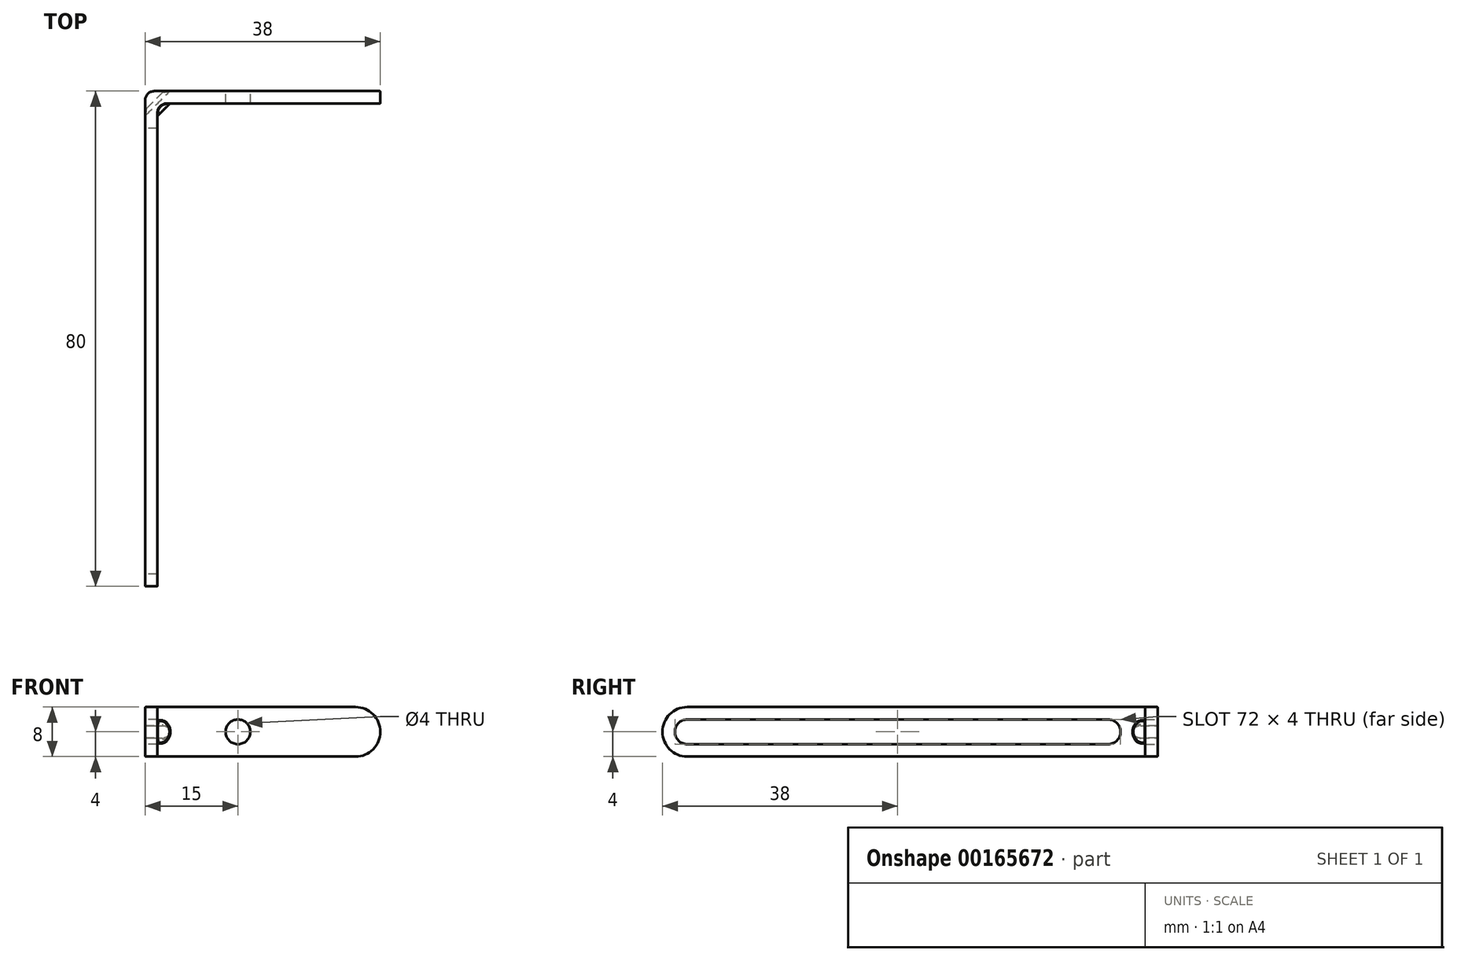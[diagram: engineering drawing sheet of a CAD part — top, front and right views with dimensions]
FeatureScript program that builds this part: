
annotation { "Feature Type Name" : "Feature", "Feature Type Description" : "" }
export const myFeature = defineFeature(function(context is Context, id is Id, definition is map)
    precondition{}
    {
        {
            var Q0;
            Q0=qCreatedBy(makeId("Top.planeOp"),FACE);
            var sketch = newSketch(context, id + "F0", { "sketchPlane" : qUnion([Q0])});
            skLineSegment(sketch, "E0", {"start": v(0, 0) * mm, "end": v(0, 80) * mm});
            skLineSegment(sketch, "E1", {"start": v(0, 80) * mm, "end": v(38, 80) * mm});
            skLineSegment(sketch, "E2.0", {"start": v(2, 78) * mm, "end": v(38, 78) * mm});
            skLineSegment(sketch, "E2.1", {"start": v(2, 0) * mm, "end": v(2, 78) * mm});
            skLineSegment(sketch, "E3", {"start": v(38, 80) * mm, "end": v(38, 78) * mm});
            skLineSegment(sketch, "E4", {"start": v(2, 0) * mm, "end": v(0, 0) * mm});
            skSolve(sketch);
        }
        {
            var Q0;
            Q0=makeQuery(id+"F0.imprint","IMPRINT",FACE,{"disambiguationData":[TD([[makeQuery(id+"F0.imprint","IMPRINT",EDGE,{"derivedFrom":sQuery(id+"F0.wireOp",EDGE,"E0")}),-1.0]])]});
            var Q1;
            Q1=sQuery(id+"F0.wireOp",EDGE,"E1");
            extrude(context, id + "F1", {"entities" : qUnion([Q0]), "surfaceEntities" : qUnion([Q1]), "endBound" : BoundingType.SYMMETRIC, "depth" : 8 * mm, "offsetDistance" : 25 * mm});
        }
        {
            var Q0;
            Q0=makeQuery(id+"F1.opExtrude","CAP_EDGE",EDGE,{"disambiguationData":[OSD([sQuery(id+"F0.wireOp",EDGE,"E4")])],"isStart":false});
            var Q1;
            Q1=makeQuery(id+"F1.opExtrude","CAP_EDGE",EDGE,{"disambiguationData":[OSD([sQuery(id+"F0.wireOp",EDGE,"E4")])],"isStart":true});
            var Q2;
            Q2=makeQuery(id+"F1.opExtrude","CAP_EDGE",EDGE,{"disambiguationData":[OSD([sQuery(id+"F0.wireOp",EDGE,"E3")])],"isStart":false});
            var Q3;
            Q3=makeQuery(id+"F1.opExtrude","CAP_EDGE",EDGE,{"disambiguationData":[OSD([sQuery(id+"F0.wireOp",EDGE,"E3")])],"isStart":true});
            fillet(context, id + "F2", {"entities" : qUnion([Q0, Q1, Q2, Q3]), "tangentPropagation" : true, "radius" : 4 * mm, "defaultsChanged" : true, "vertexSettings" : []});
        }
        {
            var Q0;
            Q0=makeQuery(id+"F1.opExtrude","SWEPT_EDGE",EDGE,{"disambiguationData":[OSD([sQuery(id+"F0.wireOp",EDGE,"E2.0"),sQuery(id+"F0.wireOp",EDGE,"E2.1")])]});
            var Q1;
            Q1=makeQuery(id+"F1.opExtrude","SWEPT_EDGE",EDGE,{"disambiguationData":[OSD([sQuery(id+"F0.wireOp",EDGE,"E0"),sQuery(id+"F0.wireOp",EDGE,"E1")])]});
            fillet(context, id + "F3", {"entities" : qUnion([Q0, Q1]), "tangentPropagation" : true, "radius" : 1.5 * mm, "defaultsChanged" : false, "vertexSettings" : []});
        }
        {
            var Q0;
            Q0=makeQuery(id+"F1.opExtrude","SWEPT_FACE",FACE,{"disambiguationData":[OSD([sQuery(id+"F0.wireOp",EDGE,"E0")])]});
            var sketch = newSketch(context, id + "F4", { "sketchPlane" : qUnion([Q0])});
            skCircle(sketch, "E5", {"center": v(-4, 0) * mm, "radius": 2 * mm});
            skCircle(sketch, "E6", {"center": v(-72, 0) * mm, "radius": 2 * mm});
            skLineSegment(sketch, "E7", {"start": v(-72, 2) * mm, "end": v(-4, 2) * mm});
            skLineSegment(sketch, "E8", {"start": v(-4, -2) * mm, "end": v(-72, -2) * mm});
            skLineSegment(sketch, "E9", {"start": v(6.38, 0) * mm, "end": v(-88.71, 0) * mm, "construction": true});
            skSolve(sketch);
        }
        {
            var Q0;
            Q0 = qSketchRegion(id + "F4", true);
            extrude(context, id + "F5", {"entities" : qUnion([Q0]), "operationType" : NewBodyOperationType.REMOVE, "endBound" : BoundingType.UP_TO_NEXT, "oppositeDirection" : true, "depth" : 25 * mm, "offsetDistance" : 25 * mm});
        }
        {
            var Q0;
            Q0=makeQuery(id+"F1.opExtrude","SWEPT_FACE",FACE,{"disambiguationData":[OSD([sQuery(id+"F0.wireOp",EDGE,"E1")])]});
            var sketch = newSketch(context, id + "F6", { "sketchPlane" : qUnion([Q0])});
            skLineSegment(sketch, "E10.bottom", {"start": v(3, 1) * mm, "end": v(-3, 1) * mm});
            skLineSegment(sketch, "E10.top", {"start": v(3, -1) * mm, "end": v(-3, -1) * mm});
            skLineSegment(sketch, "E10.left", {"start": v(4, 0) * mm, "end": v(4, 0) * mm});
            skLineSegment(sketch, "E10.right", {"start": v(-4, 0) * mm, "end": v(-4, 0) * mm});
            skPoint(sketch, "E10.middle", {"position": v(0, 0) * mm});
            skPoint(sketch, "E11.visualSharp", {"position": v(4, 1) * mm});
            skArc(sketch, "E11.filletArc", {"start": v(4, 0) * mm, "mid": v(3.7, 0.7) * mm, "end": v(3, 1) * mm});
            skPoint(sketch, "E12.visualSharp", {"position": v(-4, 1) * mm});
            skArc(sketch, "E12.filletArc", {"start": v(-3, 1) * mm, "mid": v(-3.7, 0.7) * mm, "end": v(-4, 0) * mm});
            skPoint(sketch, "E13.visualSharp", {"position": v(-4, -1) * mm});
            skArc(sketch, "E13.filletArc", {"start": v(-4, 0) * mm, "mid": v(-3.7, -0.7) * mm, "end": v(-3, -1) * mm});
            skPoint(sketch, "E14.visualSharp", {"position": v(4, -1) * mm});
            skArc(sketch, "E14.filletArc", {"start": v(3, -1) * mm, "mid": v(3.7, -0.7) * mm, "end": v(4, 0) * mm});
            skSolve(sketch);
        }
        {
            var Q0;
            Q0 = qSketchRegion(id + "F6", true);
            extrude(context, id + "F7", {"entities" : qUnion([Q0]), "oppositeDirection" : true, "depth" : 4 * mm, "offsetDistance" : 25 * mm});
        }
        {
            var Q0;
            Q0=makeQuery(id+"F7.opExtrude","CAP_EDGE",EDGE,{"disambiguationData":[OSD([sQuery(id+"F6.wireOp",EDGE,"E10.bottom")])],"isStart":false});
            var Q1;
            Q1=makeQuery(id+"F7.opExtrude","CAP_EDGE",EDGE,{"disambiguationData":[OSD([sQuery(id+"F6.wireOp",EDGE,"E10.top")])],"isStart":false});
            fillet(context, id + "F8", {"entities" : qUnion([Q0, Q1]), "radius" : 1 * mm, "defaultsChanged" : true, "vertexSettings" : []});
        }
        {
            var Q0;
            Q0=makeQuery(id+"F7.opExtrude","SWEPT_BODY",BODY,{"disambiguationData":[OSD([sQuery(id+"F6.wireOp",EDGE,"E10.bottom"),sQuery(id+"F6.wireOp",EDGE,"E10.top"),sQuery(id+"F6.wireOp",EDGE,"E11.filletArc"),sQuery(id+"F6.wireOp",EDGE,"E12.filletArc"),sQuery(id+"F6.wireOp",EDGE,"E13.filletArc"),sQuery(id+"F6.wireOp",EDGE,"E14.filletArc")])]});
            var Q1;
            Q1=makeQuery(id+"F1.opExtrude","SWEPT_BODY",BODY,{"disambiguationData":[OSD([sQuery(id+"F0.wireOp",EDGE,"E0"),sQuery(id+"F0.wireOp",EDGE,"E1"),sQuery(id+"F0.wireOp",EDGE,"E2.0"),sQuery(id+"F0.wireOp",EDGE,"E2.1"),sQuery(id+"F0.wireOp",EDGE,"E3"),sQuery(id+"F0.wireOp",EDGE,"E4")])]});
            booleanBodies(context, id + "F9", {"operationType" : BooleanOperationType.SUBTRACTION, "tools" : qUnion([Q0]), "targets" : qUnion([Q1])});
        }
        {
            var Q0;
            Q0=makeQuery(id+"F1.opExtrude","SWEPT_FACE",FACE,{"disambiguationData":[OSD([sQuery(id+"F0.wireOp",EDGE,"E0")])]});
            var sketch = newSketch(context, id + "F10", { "sketchPlane" : qUnion([Q0])});
            skArc(sketch, "E15.0", {"start": v(-77, -1) * mm, "mid": v(-76, 0) * mm, "end": v(-77, 1) * mm});
            skLineSegment(sketch, "E16", {"start": v(-77.2, 0) * mm, "end": v(-73.29, 0) * mm, "construction": true});
            skLineSegment(sketch, "E17", {"start": v(-77, 2.15) * mm, "end": v(-77, -2.41) * mm, "construction": true});
            skLineSegment(sketch, "E18", {"start": v(-77, 1) * mm, "end": v(-77, 2) * mm});
            skLineSegment(sketch, "E19", {"start": v(-77, 2) * mm, "end": v(-74.95, 2) * mm, "construction": true});
            skLineSegment(sketch, "E20", {"start": v(-77, -1) * mm, "end": v(-77, -2) * mm});
            skLineSegment(sketch, "E21", {"start": v(-77, 2) * mm, "end": v(-76, 2) * mm});
            skArc(sketch, "E22", {"start": v(-74, 0) * mm, "mid": v(-74.59, 1.41) * mm, "end": v(-76, 2) * mm});
            skArc(sketch, "E23.MirrorCS", {"start": v(-74, 0) * mm, "mid": v(-74.59, -1.41) * mm, "end": v(-76, -2) * mm});
            skLineSegment(sketch, "E24.MirrorCS", {"start": v(-77, -2) * mm, "end": v(-76, -2) * mm});
            skSolve(sketch);
        }
        {
            var Q0;
            {var subQ0=sQuery(id+"F6.wireOp",EDGE,"E12.filletArc");Q0=makeQuery(id+"F6.imprint","IMPRINT",FACE,{"disambiguationData":[TD([[makeQuery(id+"F6.imprint","IMPRINT",EDGE,{"derivedFrom":subQ0}),-1.0]])]});}
            var sketch = newSketch(context, id + "F11", { "sketchPlane" : qUnion([Q0])});
            skLineSegment(sketch, "E25", {"start": v(-3, -7.44) * mm, "end": v(-3, 4.7) * mm, "construction": true});
            skLineSegment(sketch, "E26", {"start": v(-1.82, 0) * mm, "end": v(-6.7, 0) * mm, "construction": true});
            skArc(sketch, "E27.0", {"start": v(-3, 1) * mm, "mid": v(-4, 0) * mm, "end": v(-3, -1) * mm});
            skLineSegment(sketch, "E28", {"start": v(-3, 1) * mm, "end": v(-3, 2) * mm});
            skLineSegment(sketch, "E29", {"start": v(-3, 2) * mm, "end": v(-5, 2) * mm, "construction": true});
            skLineSegment(sketch, "E30.MirrorCS", {"start": v(-3, -1) * mm, "end": v(-3, -2) * mm});
            skLineSegment(sketch, "E31", {"start": v(-3, 2) * mm, "end": v(-4, 2) * mm});
            skArc(sketch, "E32", {"start": v(-4, 2) * mm, "mid": v(-5.41, 1.41) * mm, "end": v(-6, 0) * mm});
            skArc(sketch, "E33.MirrorCS", {"start": v(-4, -2) * mm, "mid": v(-5.41, -1.41) * mm, "end": v(-6, 0) * mm});
            skLineSegment(sketch, "E34.MirrorCS", {"start": v(-3, -2) * mm, "end": v(-4, -2) * mm});
            skLineSegment(sketch, "E35.MirrorCS", {"start": v(-3, -2) * mm, "end": v(-5, -2) * mm, "construction": true});
            skArc(sketch, "E36.MirrorCS", {"start": v(-3, -1) * mm, "mid": v(-4, 0) * mm, "end": v(-3, 1) * mm});
            skLineSegment(sketch, "E37.MirrorCS", {"start": v(-3, 7.44) * mm, "end": v(-3, -4.7) * mm, "construction": true});
            skSolve(sketch);
        }
        {
            var Q0;
            Q0=makeQuery(id+"F10.imprint","IMPRINT",FACE,{"disambiguationData":[TD([[makeQuery(id+"F10.imprint","IMPRINT",EDGE,{"derivedFrom":sQuery(id+"F10.wireOp",EDGE,"E15.0")}),-1.0]])]});
            var Q1;
            {var subQ0=sQuery(id+"F11.wireOp",EDGE,"E28");Q1=makeQuery(id+"F11.imprint","IMPRINT",FACE,{"disambiguationData":[TD([[makeQuery(id+"F11.imprint","IMPRINT",EDGE,{"derivedFrom":subQ0}),1.0]])]});}
            var Q2;
            Q2=sQuery(id+"FDlQtbDI0yLmQig_1.wireOp",EDGE,"mHh4oXX2-Cw2Y-65nT-yoMM-4e8h4DFZw104");
            var Q3;
            Q3=sQuery(id+"F11.wireOp",VERTEX,"E27.0.end");
            var Q4;
            Q4=sQuery(id+"F10.wireOp",VERTEX,"E15.0.start");
            loft(context, id + "F12", {"operationType" : NewBodyOperationType.ADD, "sheetProfilesArray" : [{ "sheetProfileEntities" : qUnion([Q0]) }, { "sheetProfileEntities" : qUnion([Q1]) }], "guidesArray" : [{ "guideEntities" : qUnion([Q2]), "guideDerivativeType" : LoftGuideDerivativeType.DEFAULT, "guideDerivativeMagnitude" : 1 }], "matchVertices" : true, "vertices" : qUnion([Q3, Q4])});
        }
        {
            var Q0;
            Q0=makeQuery(id+"F1.opExtrude","CAP_EDGE",EDGE,{"disambiguationData":[OSD([sQuery(id+"F0.wireOp",EDGE,"E0")])],"isStart":true});
            var Q1;
            {var subQ0=sQuery(id+"F0.wireOp",EDGE,"E1");var subQ1=sQuery(id+"F0.wireOp",EDGE,"E0");Q1=makeQuery(id+"F3.opFillet","BLEND_EDGE",EDGE,{"blendedFrom":[makeQuery(id+"F1.opExtrude","SWEPT_EDGE",EDGE,{"disambiguationData":[OSD([subQ1,subQ0])]}),makeQuery(id+"F1.opExtrude","CAP_FACE",FACE,{"disambiguationData":[OSD([subQ1,subQ0,sQuery(id+"F0.wireOp",EDGE,"E2.0"),sQuery(id+"F0.wireOp",EDGE,"E2.1"),sQuery(id+"F0.wireOp",EDGE,"E3"),sQuery(id+"F0.wireOp",EDGE,"E4")])],"isStart":true})],"blendedInto":[makeQuery(id+"F1.opExtrude","CAP_FACE",FACE,{"disambiguationData":[OSD([subQ1,subQ0,sQuery(id+"F0.wireOp",EDGE,"E2.0"),sQuery(id+"F0.wireOp",EDGE,"E2.1"),sQuery(id+"F0.wireOp",EDGE,"E3"),sQuery(id+"F0.wireOp",EDGE,"E4")])],"isStart":true})]});}
            var Q2;
            Q2=makeQuery(id+"F1.opExtrude","CAP_EDGE",EDGE,{"disambiguationData":[OSD([sQuery(id+"F0.wireOp",EDGE,"E1")])],"isStart":true});
            var Q3;
            Q3=makeQuery(id+"F2.opFillet","BLEND_EDGE",EDGE,{"blendedFrom":[makeQuery(id+"F1.opExtrude","CAP_EDGE",EDGE,{"disambiguationData":[OSD([sQuery(id+"F0.wireOp",EDGE,"E3")])],"isStart":true}),makeQuery(id+"F1.opExtrude","SWEPT_FACE",FACE,{"disambiguationData":[OSD([sQuery(id+"F0.wireOp",EDGE,"E1")])]})],"blendedInto":[makeQuery(id+"F1.opExtrude","SWEPT_FACE",FACE,{"disambiguationData":[OSD([sQuery(id+"F0.wireOp",EDGE,"E1")])]})]});
            var Q4;
            Q4=makeQuery(id+"F1.opExtrude","CAP_EDGE",EDGE,{"disambiguationData":[OSD([sQuery(id+"F0.wireOp",EDGE,"E1")])],"isStart":false});
            var Q5;
            {var subQ0=sQuery(id+"F0.wireOp",EDGE,"E1");var subQ1=sQuery(id+"F0.wireOp",EDGE,"E0");Q5=makeQuery(id+"F3.opFillet","BLEND_EDGE",EDGE,{"blendedFrom":[makeQuery(id+"F1.opExtrude","SWEPT_EDGE",EDGE,{"disambiguationData":[OSD([subQ1,subQ0])]}),makeQuery(id+"F1.opExtrude","CAP_FACE",FACE,{"disambiguationData":[OSD([subQ1,subQ0,sQuery(id+"F0.wireOp",EDGE,"E2.0"),sQuery(id+"F0.wireOp",EDGE,"E2.1"),sQuery(id+"F0.wireOp",EDGE,"E3"),sQuery(id+"F0.wireOp",EDGE,"E4")])],"isStart":false})],"blendedInto":[makeQuery(id+"F1.opExtrude","CAP_FACE",FACE,{"disambiguationData":[OSD([subQ1,subQ0,sQuery(id+"F0.wireOp",EDGE,"E2.0"),sQuery(id+"F0.wireOp",EDGE,"E2.1"),sQuery(id+"F0.wireOp",EDGE,"E3"),sQuery(id+"F0.wireOp",EDGE,"E4")])],"isStart":false})]});}
            var Q6;
            Q6=makeQuery(id+"F1.opExtrude","CAP_EDGE",EDGE,{"disambiguationData":[OSD([sQuery(id+"F0.wireOp",EDGE,"E0")])],"isStart":false});
            var Q7;
            Q7=makeQuery(id+"F2.opFillet","BLEND_EDGE",EDGE,{"blendedFrom":[makeQuery(id+"F1.opExtrude","CAP_EDGE",EDGE,{"disambiguationData":[OSD([sQuery(id+"F0.wireOp",EDGE,"E4")])],"isStart":true}),makeQuery(id+"F1.opExtrude","SWEPT_FACE",FACE,{"disambiguationData":[OSD([sQuery(id+"F0.wireOp",EDGE,"E0")])]})],"blendedInto":[makeQuery(id+"F1.opExtrude","SWEPT_FACE",FACE,{"disambiguationData":[OSD([sQuery(id+"F0.wireOp",EDGE,"E0")])]})]});
            var Q8;
            Q8=makeQuery(id+"F1.opExtrude","CAP_EDGE",EDGE,{"disambiguationData":[OSD([sQuery(id+"F0.wireOp",EDGE,"E2.1")])],"isStart":true});
            var Q9;
            Q9=makeQuery(id+"F2.opFillet","BLEND_EDGE",EDGE,{"blendedFrom":[makeQuery(id+"F1.opExtrude","CAP_EDGE",EDGE,{"disambiguationData":[OSD([sQuery(id+"F0.wireOp",EDGE,"E4")])],"isStart":true}),makeQuery(id+"F1.opExtrude","SWEPT_FACE",FACE,{"disambiguationData":[OSD([sQuery(id+"F0.wireOp",EDGE,"E2.1")])]})],"blendedInto":[makeQuery(id+"F1.opExtrude","SWEPT_FACE",FACE,{"disambiguationData":[OSD([sQuery(id+"F0.wireOp",EDGE,"E2.1")])]})]});
            var Q10;
            Q10=makeQuery(id+"F1.opExtrude","CAP_EDGE",EDGE,{"disambiguationData":[OSD([sQuery(id+"F0.wireOp",EDGE,"E2.1")])],"isStart":false});
            var Q11;
            {var subQ0=sQuery(id+"F0.wireOp",EDGE,"E2.1");var subQ1=sQuery(id+"F0.wireOp",EDGE,"E2.0");Q11=makeQuery(id+"F3.opFillet","BLEND_EDGE",EDGE,{"blendedFrom":[makeQuery(id+"F1.opExtrude","SWEPT_EDGE",EDGE,{"disambiguationData":[OSD([subQ1,subQ0])]}),makeQuery(id+"F1.opExtrude","CAP_FACE",FACE,{"disambiguationData":[OSD([sQuery(id+"F0.wireOp",EDGE,"E0"),sQuery(id+"F0.wireOp",EDGE,"E1"),subQ1,subQ0,sQuery(id+"F0.wireOp",EDGE,"E3"),sQuery(id+"F0.wireOp",EDGE,"E4")])],"isStart":false})],"blendedInto":[makeQuery(id+"F1.opExtrude","CAP_FACE",FACE,{"disambiguationData":[OSD([sQuery(id+"F0.wireOp",EDGE,"E0"),sQuery(id+"F0.wireOp",EDGE,"E1"),subQ1,subQ0,sQuery(id+"F0.wireOp",EDGE,"E3"),sQuery(id+"F0.wireOp",EDGE,"E4")])],"isStart":false})]});}
            var Q12;
            Q12=makeQuery(id+"F1.opExtrude","CAP_EDGE",EDGE,{"disambiguationData":[OSD([sQuery(id+"F0.wireOp",EDGE,"E2.0")])],"isStart":false});
            var Q13;
            Q13=makeQuery(id+"F2.opFillet","BLEND_EDGE",EDGE,{"blendedFrom":[makeQuery(id+"F1.opExtrude","CAP_EDGE",EDGE,{"disambiguationData":[OSD([sQuery(id+"F0.wireOp",EDGE,"E3")])],"isStart":true}),makeQuery(id+"F1.opExtrude","SWEPT_FACE",FACE,{"disambiguationData":[OSD([sQuery(id+"F0.wireOp",EDGE,"E2.0")])]})],"blendedInto":[makeQuery(id+"F1.opExtrude","SWEPT_FACE",FACE,{"disambiguationData":[OSD([sQuery(id+"F0.wireOp",EDGE,"E2.0")])]})]});
            var Q14;
            Q14=makeQuery(id+"F1.opExtrude","CAP_EDGE",EDGE,{"disambiguationData":[OSD([sQuery(id+"F0.wireOp",EDGE,"E2.0")])],"isStart":true});
            var Q15;
            {var subQ0=sQuery(id+"F0.wireOp",EDGE,"E2.1");var subQ1=sQuery(id+"F0.wireOp",EDGE,"E2.0");Q15=makeQuery(id+"F3.opFillet","BLEND_EDGE",EDGE,{"blendedFrom":[makeQuery(id+"F1.opExtrude","SWEPT_EDGE",EDGE,{"disambiguationData":[OSD([subQ1,subQ0])]}),makeQuery(id+"F1.opExtrude","CAP_FACE",FACE,{"disambiguationData":[OSD([sQuery(id+"F0.wireOp",EDGE,"E0"),sQuery(id+"F0.wireOp",EDGE,"E1"),subQ1,subQ0,sQuery(id+"F0.wireOp",EDGE,"E3"),sQuery(id+"F0.wireOp",EDGE,"E4")])],"isStart":true})],"blendedInto":[makeQuery(id+"F1.opExtrude","CAP_FACE",FACE,{"disambiguationData":[OSD([sQuery(id+"F0.wireOp",EDGE,"E0"),sQuery(id+"F0.wireOp",EDGE,"E1"),subQ1,subQ0,sQuery(id+"F0.wireOp",EDGE,"E3"),sQuery(id+"F0.wireOp",EDGE,"E4")])],"isStart":true})]});}
            fillet(context, id + "F13", {"entities" : qUnion([Q0, Q1, Q2, Q3, Q4, Q5, Q6, Q7, Q8, Q9, Q10, Q11, Q12, Q13, Q14, Q15]), "radius" : 0.1 * mm, "defaultsChanged" : false, "vertexSettings" : []});
        }
        {
            var Q0;
            Q0=makeQuery(id+"F9.opBoolean","INTERSECT",EDGE,{"derivedFrom":[makeQuery(id+"F3.opFillet","BLEND_FACE",FACE,{"disambiguationData":[OSD([sQuery(id+"F0.wireOp",EDGE,"E0"),sQuery(id+"F0.wireOp",EDGE,"E1")])]}),makeQuery(id+"F7.opExtrude","SWEPT_FACE",FACE,{"disambiguationData":[OSD([sQuery(id+"F6.wireOp",EDGE,"E10.bottom")])]})]});
            fillet(context, id + "F14", {"entities" : qUnion([Q0]), "tangentPropagation" : true, "radius" : 0.2 * mm, "defaultsChanged" : true, "vertexSettings" : []});
        }
        {
            var Q0;
            Q0=makeQuery(id+"F12.boolean.opBoolean","INTERSECT",EDGE,{"derivedFrom":[makeQuery(id+"F1.opExtrude","SWEPT_FACE",FACE,{"disambiguationData":[OSD([sQuery(id+"F0.wireOp",EDGE,"E2.0")])]}),makeQuery(id+"F12.opLoft","SWEPT_FACE",FACE,{"disambiguationData":[OSD([sQuery(id+"F10.wireOp",EDGE,"E21"),sQuery(id+"F10.wireOp",EDGE,"E22"),sQuery(id+"F10.wireOp",EDGE,"E23.MirrorCS"),sQuery(id+"F10.wireOp",EDGE,"E24.MirrorCS"),sQuery(id+"F11.wireOp",EDGE,"E31"),sQuery(id+"F11.wireOp",EDGE,"E32"),sQuery(id+"F11.wireOp",EDGE,"E33.MirrorCS"),sQuery(id+"F11.wireOp",EDGE,"E34.MirrorCS")])]})]});
            fillet(context, id + "F15", {"entities" : qUnion([Q0]), "tangentPropagation" : true, "radius" : 0.2 * mm, "defaultsChanged" : true, "vertexSettings" : []});
        }
        {
            var Q0;
            Q0=makeQuery(id+"F1.opExtrude","SWEPT_FACE",FACE,{"disambiguationData":[OSD([sQuery(id+"F0.wireOp",EDGE,"E1")])]});
            var sketch = newSketch(context, id + "F16", { "sketchPlane" : qUnion([Q0])});
            skCircle(sketch, "E38", {"center": v(-15, 0) * mm, "radius": 2 * mm});
            skPoint(sketch, "E39", {"position": v(-17.75, -3.9) * mm});
            skLineSegment(sketch, "E40", {"start": v(-34, 0) * mm, "end": v(-15, 0) * mm, "construction": true});
            skPoint(sketch, "E41", {"position": v(-24.5, 0) * mm});
            skSolve(sketch);
        }
        {
            var Q0;
            Q0 = qSketchRegion(id + "F16", true);
            extrude(context, id + "F17", {"entities" : qUnion([Q0]), "operationType" : NewBodyOperationType.REMOVE, "endBound" : BoundingType.UP_TO_NEXT, "oppositeDirection" : true, "depth" : 25 * mm, "offsetDistance" : 25 * mm});
        }
    });
